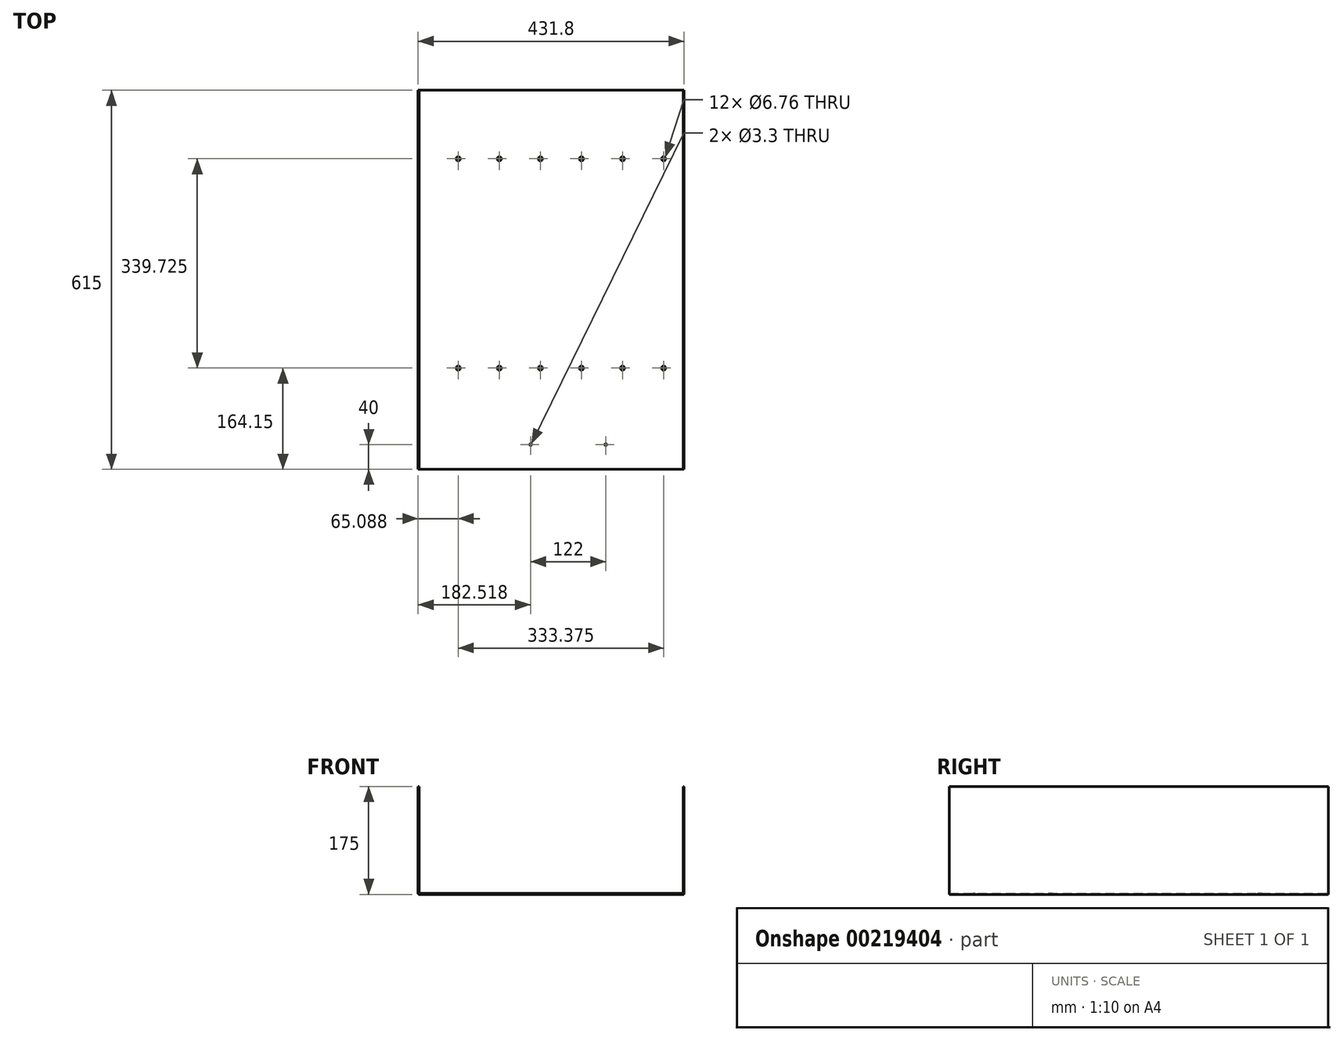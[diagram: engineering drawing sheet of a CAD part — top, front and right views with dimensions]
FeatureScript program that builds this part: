
annotation { "Feature Type Name" : "Feature", "Feature Type Description" : "" }
export const myFeature = defineFeature(function(context is Context, id is Id, definition is map)
    precondition{}
    {
        {
            var Q0;
            Q0=qCreatedBy(makeId("Top.planeOp"),FACE);
            var sketch = newSketch(context, id + "F0", { "sketchPlane" : qUnion([Q0])});
            skLineSegment(sketch, "E0.bottom", {"start": v(-215.9, -307.5) * mm, "end": v(215.9, -307.5) * mm});
            skLineSegment(sketch, "E0.top", {"start": v(-215.9, 307.5) * mm, "end": v(215.9, 307.5) * mm});
            skLineSegment(sketch, "E0.left", {"start": v(-215.9, -307.5) * mm, "end": v(-215.9, 307.5) * mm});
            skLineSegment(sketch, "E0.right", {"start": v(215.9, -307.5) * mm, "end": v(215.9, 307.5) * mm});
            skPoint(sketch, "E0.middle", {"position": v(0, 0) * mm});
            skSolve(sketch);
        }
        {
            var Q0;
            Q0=qSketchRegion(id+"F0",true);
            extrude(context, id + "F1", {"entities" : qUnion([Q0]), "oppositeDirection" : true, "depth" : 1.5 * mm});
        }
        {
            var Q0;
            Q0=makeQuery(id+"F1.opExtrude","SWEPT_FACE",FACE,{"disambiguationData":[OSD([sQuery(id+"F0.wireOp",EDGE,"E0.left")])]});
            var sketch = newSketch(context, id + "F2", { "sketchPlane" : qUnion([Q0])});
            skLineSegment(sketch, "E1.bottom", {"start": v(-307.5, -1.5) * mm, "end": v(307.5, -1.5) * mm});
            skLineSegment(sketch, "E1.top", {"start": v(-307.5, 173.5) * mm, "end": v(307.5, 173.5) * mm});
            skLineSegment(sketch, "E1.left", {"start": v(-307.5, -1.5) * mm, "end": v(-307.5, 173.5) * mm});
            skLineSegment(sketch, "E1.right", {"start": v(307.5, -1.5) * mm, "end": v(307.5, 173.5) * mm});
            skSolve(sketch);
        }
        {
            var Q0;
            {var subQ0=sQuery(id+"F2.wireOp",EDGE,"E1.top");Q0=makeQuery(id+"F2.imprint","IMPRINT",FACE,{"disambiguationData":[TD([[makeQuery(id+"F2.imprint","IMPRINT",EDGE,{"derivedFrom":subQ0}),-1.0]])]});}
            extrude(context, id + "F3", {"entities" : qUnion([Q0]), "operationType" : NewBodyOperationType.ADD, "oppositeDirection" : true, "depth" : 1.5 * mm});
        }
        {
            var Q0;
            Q0=makeQuery(id+"F1.opExtrude","SWEPT_FACE",FACE,{"disambiguationData":[OSD([sQuery(id+"F0.wireOp",EDGE,"E0.right")])]});
            var sketch = newSketch(context, id + "F4", { "sketchPlane" : qUnion([Q0])});
            skLineSegment(sketch, "E2.bottom", {"start": v(-307.5, -1.5) * mm, "end": v(307.5, -1.5) * mm});
            skLineSegment(sketch, "E2.top", {"start": v(-307.5, 173.5) * mm, "end": v(307.5, 173.5) * mm});
            skLineSegment(sketch, "E2.left", {"start": v(-307.5, -1.5) * mm, "end": v(-307.5, 173.5) * mm});
            skLineSegment(sketch, "E2.right", {"start": v(307.5, -1.5) * mm, "end": v(307.5, 173.5) * mm});
            skSolve(sketch);
        }
        {
            var Q0;
            {var subQ0=sQuery(id+"F4.wireOp",EDGE,"E2.top");Q0=makeQuery(id+"F4.imprint","IMPRINT",FACE,{"disambiguationData":[TD([[makeQuery(id+"F4.imprint","IMPRINT",EDGE,{"derivedFrom":subQ0}),-1.0]])]});}
            extrude(context, id + "F5", {"entities" : qUnion([Q0]), "operationType" : NewBodyOperationType.ADD, "oppositeDirection" : true, "depth" : 1.5 * mm});
        }
        {
            var Q0;
            Q0=makeQuery(id+"F1.opExtrude","CAP_EDGE",EDGE,{"disambiguationData":[OSD([sQuery(id+"F0.wireOp",EDGE,"E0.left")])],"isStart":false});
            var Q1;
            Q1=makeQuery(id+"F1.opExtrude","CAP_EDGE",EDGE,{"disambiguationData":[OSD([sQuery(id+"F0.wireOp",EDGE,"E0.right")])],"isStart":false});
            fillet(context, id + "F6", {"entities" : qUnion([Q0, Q1]), "radius" : 1.5 * mm, "tangentPropagation" : true, "allowEdgeOverflow" : false});
        }
        {
            var Q0;
            Q0=makeQuery(id+"F1.opExtrude","CAP_FACE",FACE,{"disambiguationData":[OSD([sQuery(id+"F0.wireOp",EDGE,"E0.bottom"),sQuery(id+"F0.wireOp",EDGE,"E0.top"),sQuery(id+"F0.wireOp",EDGE,"E0.left"),sQuery(id+"F0.wireOp",EDGE,"E0.right")])],"isStart":false});
            var sketch = newSketch(context, id + "F7", { "sketchPlane" : qUnion([Q0])});
            skPoint(sketch, "E3", {"position": v(182.56, -196.37) * mm});
            skPoint(sketch, "E4", {"position": v(115.89, -196.38) * mm});
            skPoint(sketch, "E5", {"position": v(49.21, -196.38) * mm});
            skPoint(sketch, "E6", {"position": v(-17.46, -196.38) * mm});
            skPoint(sketch, "E7", {"position": v(-84.14, -196.38) * mm});
            skPoint(sketch, "E8", {"position": v(182.56, 143.35) * mm});
            skPoint(sketch, "E9", {"position": v(115.89, 143.35) * mm});
            skPoint(sketch, "E10", {"position": v(49.21, 143.35) * mm});
            skPoint(sketch, "E11", {"position": v(-17.46, 143.35) * mm});
            skPoint(sketch, "E12", {"position": v(-84.14, 143.35) * mm});
            skPoint(sketch, "E13", {"position": v(-150.81, -196.38) * mm});
            skPoint(sketch, "E14", {"position": v(-150.81, 143.35) * mm});
            skPoint(sketch, "E15", {"position": v(-33.38, 267.5) * mm});
            skPoint(sketch, "E16", {"position": v(88.62, 267.5) * mm});
            skSolve(sketch);
        }
        {
            var Q0;
            Q0=sQuery(id+"F7.wireOp",VERTEX,"E12");
            var Q1;
            Q1=sQuery(id+"F7.wireOp",VERTEX,"E11");
            var Q2;
            Q2=sQuery(id+"F7.wireOp",VERTEX,"E10");
            var Q3;
            Q3=sQuery(id+"F7.wireOp",VERTEX,"E9");
            var Q4;
            Q4=sQuery(id+"F7.wireOp",VERTEX,"E8");
            var Q5;
            Q5=sQuery(id+"F7.wireOp",VERTEX,"E3");
            var Q6;
            Q6=sQuery(id+"F7.wireOp",VERTEX,"E4");
            var Q7;
            Q7=sQuery(id+"F7.wireOp",VERTEX,"E5");
            var Q8;
            Q8=sQuery(id+"F7.wireOp",VERTEX,"E6");
            var Q9;
            Q9=sQuery(id+"F7.wireOp",VERTEX,"E7");
            var Q10;
            Q10=sQuery(id+"F7.wireOp",VERTEX,"E13");
            var Q11;
            Q11=sQuery(id+"F7.wireOp",VERTEX,"E14");
            var Q12;
            Q12=makeQuery(id+"F1.opExtrude","SWEPT_BODY",BODY,{"disambiguationData":[OSD([sQuery(id+"F0.wireOp",EDGE,"E0.bottom"),sQuery(id+"F0.wireOp",EDGE,"E0.top"),sQuery(id+"F0.wireOp",EDGE,"E0.left"),sQuery(id+"F0.wireOp",EDGE,"E0.right")])]});
            hole(context, id + "F8", {"style" : HoleStyle.SIMPLE, "endStyle" : HoleEndStyle.THROUGH, "standardTappedOrClearance" : lookupTablePath({ "standard" : "ANSI", "fit" : "Normal (ASME)", "size" : "1/4", "type" : "Clearance" }), "standardBlindInLast" : lookupTablePath({ "fit" : "Free", "standard" : "ANSI", "size" : "1/4", "type" : "Clearance" }), "holeDiameter" : 6.76 * mm, "locations" : qUnion([Q0, Q1, Q2, Q3, Q4, Q5, Q6, Q7, Q8, Q9, Q10, Q11]), "scope" : qUnion([Q12]), "majorDiameter" : 6.35 * mm, "tappedDepth" : 12.7 * mm, "tapClearance" : 3, "startStyle" : HoleStartStyle.SKETCH});
        }
        {
            var Q0;
            Q0=sQuery(id+"F7.wireOp",VERTEX,"E15");
            var Q1;
            Q1=sQuery(id+"F7.wireOp",VERTEX,"E16");
            var Q2;
            Q2=makeQuery(id+"F1.opExtrude","SWEPT_BODY",BODY,{"disambiguationData":[OSD([sQuery(id+"F0.wireOp",EDGE,"E0.bottom"),sQuery(id+"F0.wireOp",EDGE,"E0.top"),sQuery(id+"F0.wireOp",EDGE,"E0.left"),sQuery(id+"F0.wireOp",EDGE,"E0.right")])]});
            hole(context, id + "F9", {"style" : HoleStyle.SIMPLE, "endStyle" : HoleEndStyle.THROUGH, "standardTappedOrClearance" : lookupTablePath({ "standard" : "ISO", "fit" : "Normal", "size" : "M3", "type" : "Clearance" }), "standardBlindInLast" : lookupTablePath({ "fit" : "Standard", "standard" : "ISO", "size" : "M3", "type" : "Clearance" }), "holeDiameter" : 3.3 * mm, "majorDiameter" : 6.35 * mm, "tappedDepth" : 12.7 * mm, "tapClearance" : 3, "locations" : qUnion([Q0, Q1]), "scope" : qUnion([Q2]), "startStyle" : HoleStartStyle.SKETCH});
        }
    });
